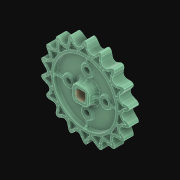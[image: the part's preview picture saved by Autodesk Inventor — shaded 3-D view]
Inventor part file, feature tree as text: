
AUTODESK INVENTOR PART (.ipt)
format: ipt  version: 2021 (Build 250183000, 183)  size: 3,632,640 bytes
history: native  units: in
note: dims shown in document units (in); Inventor stores cm internally (conversion verified against a paired STEP export)
features: sketch x1, other x1, chamfer x1, extrude x1
ambient origin geometry x8: Origin, YZ Plane, XZ Plane, XY Plane, X Axis, Y Axis, Z Axis, Center Point
bodies: Solid1 (feature_tree)
feature tree (4):
  sketch  "Sketch1"
  other  "Srf1"
  chamfer  "Chamfer1"  Distance=0.3937in
  extrude  "ExtrusionSrf1"  [1 undecoded]
note: 1 required parameter value undecoded (feature->parameter linkage not recoverable at this tier; creation-order binding heuristic only, values carry confidence <= 0.55)
